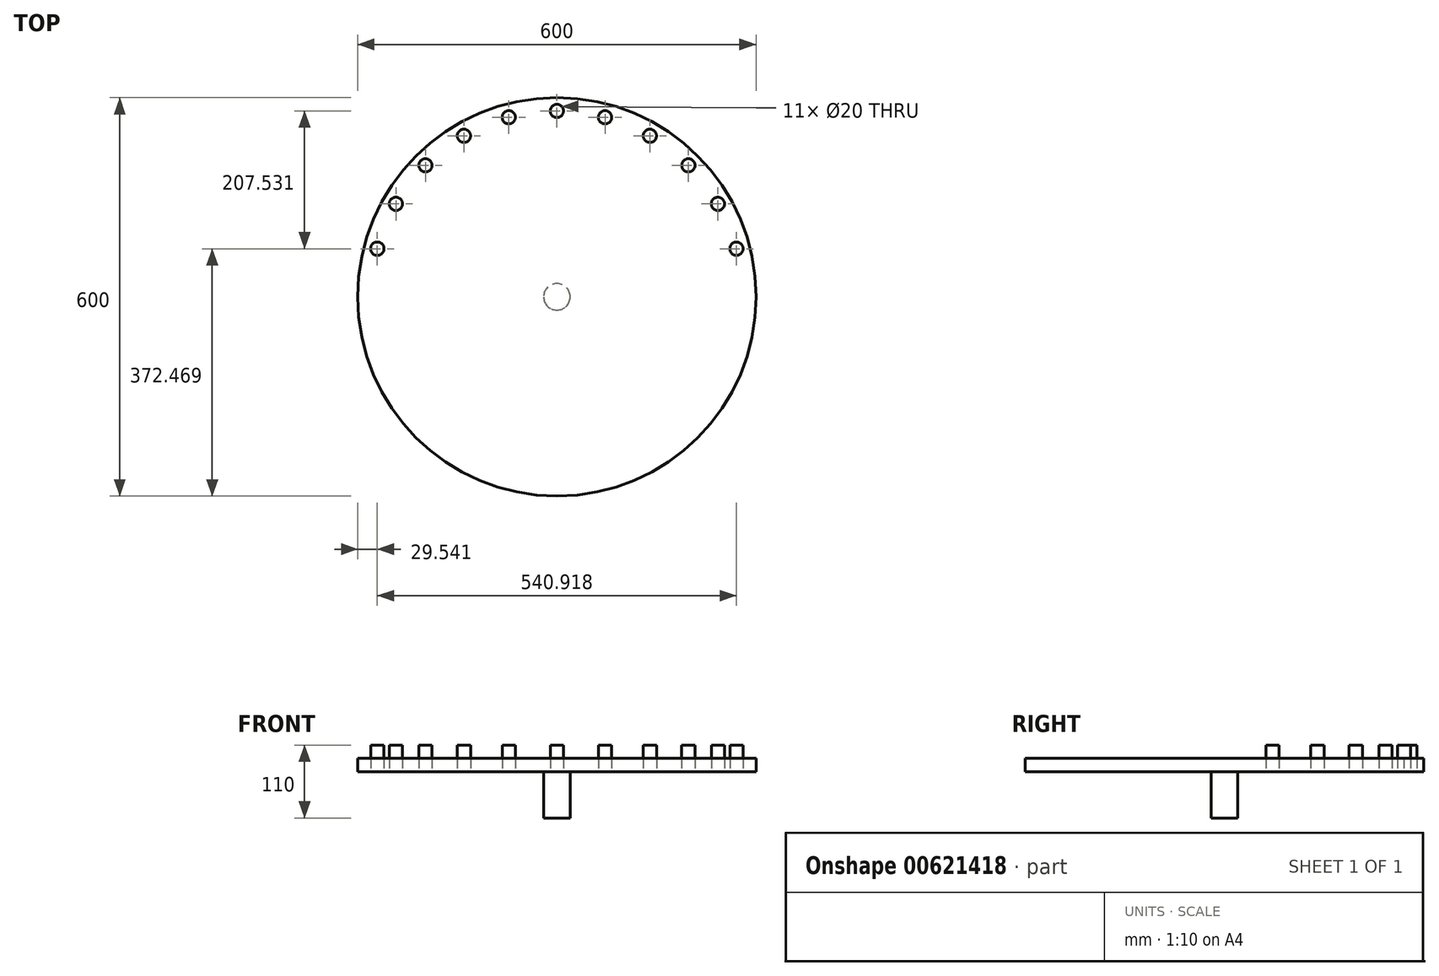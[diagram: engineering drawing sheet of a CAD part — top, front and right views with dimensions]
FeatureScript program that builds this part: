
annotation { "Feature Type Name" : "Feature", "Feature Type Description" : "" }
export const myFeature = defineFeature(function(context is Context, id is Id, definition is map)
    precondition{}
    {
        {
            var Q0;
            Q0=qCreatedBy(makeId("Top.planeOp"),FACE);
            var sketch = newSketch(context, id + "F0", { "sketchPlane" : qUnion([Q0])});
            skCircle(sketch, "E0", {"center": v(0, 0) * mm, "radius": 300 * mm});
            skCircle(sketch, "E1.0", {"center": v(0, 0) * mm, "radius": 280 * mm, "construction": true});
            skLineSegment(sketch, "E2", {"start": v(0, 0) * mm, "end": v(-300, 0) * mm, "construction": true});
            skLineSegment(sketch, "E3", {"start": v(0, 0) * mm, "end": v(-270.46, 72.47) * mm, "construction": true});
            skLineSegment(sketch, "E4", {"start": v(0, 0) * mm, "end": v(-242.49, 140) * mm, "construction": true});
            skLineSegment(sketch, "E5", {"start": v(0, 0) * mm, "end": v(-197.99, 197.99) * mm, "construction": true});
            skLineSegment(sketch, "E6", {"start": v(0, 0) * mm, "end": v(-140, 242.49) * mm, "construction": true});
            skLineSegment(sketch, "E7", {"start": v(0, 0) * mm, "end": v(-72.47, 270.46) * mm, "construction": true});
            skLineSegment(sketch, "E8", {"start": v(0, 0) * mm, "end": v(0, 280) * mm, "construction": true});
            skLineSegment(sketch, "E9.MirrorCS", {"start": v(0, 0) * mm, "end": v(72.47, 270.46) * mm, "construction": true});
            skLineSegment(sketch, "E10.MirrorCS", {"start": v(0, 0) * mm, "end": v(140, 242.49) * mm, "construction": true});
            skLineSegment(sketch, "E11.MirrorCS", {"start": v(0, 0) * mm, "end": v(197.99, 197.99) * mm, "construction": true});
            skLineSegment(sketch, "E12.MirrorCS", {"start": v(0, 0) * mm, "end": v(242.49, 140) * mm, "construction": true});
            skLineSegment(sketch, "E13.MirrorCS", {"start": v(0, 0) * mm, "end": v(270.46, 72.47) * mm, "construction": true});
            skLineSegment(sketch, "E14.MirrorCS", {"start": v(0, 0) * mm, "end": v(300, 0) * mm, "construction": true});
            skCircle(sketch, "E15", {"center": v(-270.46, 72.47) * mm, "radius": 10 * mm});
            skCircle(sketch, "E16", {"center": v(-242.49, 140) * mm, "radius": 10 * mm});
            skCircle(sketch, "E17", {"center": v(-197.99, 197.99) * mm, "radius": 10 * mm});
            skCircle(sketch, "E18", {"center": v(-140, 242.49) * mm, "radius": 10 * mm});
            skCircle(sketch, "E19", {"center": v(-72.47, 270.46) * mm, "radius": 10 * mm});
            skCircle(sketch, "E20", {"center": v(0, 280) * mm, "radius": 10 * mm});
            skCircle(sketch, "E21.MirrorC", {"center": v(270.46, 72.47) * mm, "radius": 10 * mm});
            skCircle(sketch, "E22.MirrorC", {"center": v(242.49, 140) * mm, "radius": 10 * mm});
            skCircle(sketch, "E23.MirrorC", {"center": v(197.99, 197.99) * mm, "radius": 10 * mm});
            skCircle(sketch, "E24.MirrorC", {"center": v(140, 242.49) * mm, "radius": 10 * mm});
            skCircle(sketch, "E25.MirrorC", {"center": v(72.47, 270.46) * mm, "radius": 10 * mm});
            skCircle(sketch, "E26", {"center": v(0, 0) * mm, "radius": 20 * mm});
            skSolve(sketch);
        }
        {
            var Q0;
            Q0=makeQuery(id+"F0.imprint","IMPRINT",FACE,{"disambiguationData":[TD([[makeQuery(id+"F0.imprint","IMPRINT",EDGE,{"derivedFrom":sQuery(id+"F0.wireOp",EDGE,"E0")}),1.0]])]});
            var Q1;
            Q1=sQuery(id+"F0.wireOp",EDGE,"E0");
            extrude(context, id + "F1", {"entities" : qUnion([Q0]), "surfaceEntities" : qUnion([Q1]), "depth" : 20 * mm, "offsetDistance" : 25 * mm});
        }
        {
            var Q0;
            Q0=makeQuery(id+"F1.opExtrude","CAP_FACE",FACE,{"disambiguationData":[OSD([sQuery(id+"F0.wireOp",EDGE,"E0"),sQuery(id+"F0.wireOp",EDGE,"E15"),sQuery(id+"F0.wireOp",EDGE,"E16"),sQuery(id+"F0.wireOp",EDGE,"E17"),sQuery(id+"F0.wireOp",EDGE,"E18"),sQuery(id+"F0.wireOp",EDGE,"E19"),sQuery(id+"F0.wireOp",EDGE,"E20"),sQuery(id+"F0.wireOp",EDGE,"E21.MirrorC"),sQuery(id+"F0.wireOp",EDGE,"E22.MirrorC"),sQuery(id+"F0.wireOp",EDGE,"E23.MirrorC"),sQuery(id+"F0.wireOp",EDGE,"E24.MirrorC"),sQuery(id+"F0.wireOp",EDGE,"E25.MirrorC"),sQuery(id+"F0.wireOp",EDGE,"E26")])],"isStart":false});
            var sketch = newSketch(context, id + "F2", { "sketchPlane" : qUnion([Q0])});
            skCircle(sketch, "E27.0", {"center": v(0, 0) * mm, "radius": 280 * mm, "construction": true});
            skLineSegment(sketch, "E28", {"start": v(0, 0) * mm, "end": v(-300, 0) * mm, "construction": true});
            skLineSegment(sketch, "E29", {"start": v(0, 0) * mm, "end": v(-270.46, 72.47) * mm, "construction": true});
            skLineSegment(sketch, "E30", {"start": v(0, 0) * mm, "end": v(-242.49, 140) * mm, "construction": true});
            skLineSegment(sketch, "E31", {"start": v(0, 0) * mm, "end": v(-197.99, 197.99) * mm, "construction": true});
            skLineSegment(sketch, "E32", {"start": v(0, 0) * mm, "end": v(-140, 242.49) * mm, "construction": true});
            skLineSegment(sketch, "E33", {"start": v(0, 0) * mm, "end": v(-72.47, 270.46) * mm, "construction": true});
            skLineSegment(sketch, "E34", {"start": v(0, 0) * mm, "end": v(0, 280) * mm, "construction": true});
            skLineSegment(sketch, "E35.MirrorCS", {"start": v(0, 0) * mm, "end": v(72.47, 270.46) * mm, "construction": true});
            skLineSegment(sketch, "E36.MirrorCS", {"start": v(0, 0) * mm, "end": v(140, 242.49) * mm, "construction": true});
            skLineSegment(sketch, "E37.MirrorCS", {"start": v(0, 0) * mm, "end": v(197.99, 197.99) * mm, "construction": true});
            skLineSegment(sketch, "E38.MirrorCS", {"start": v(0, 0) * mm, "end": v(242.49, 140) * mm, "construction": true});
            skLineSegment(sketch, "E39.MirrorCS", {"start": v(0, 0) * mm, "end": v(270.46, 72.47) * mm, "construction": true});
            skLineSegment(sketch, "E40.MirrorCS", {"start": v(0, 0) * mm, "end": v(300, 0) * mm, "construction": true});
            skCircle(sketch, "E41", {"center": v(-270.46, 72.47) * mm, "radius": 10 * mm});
            skCircle(sketch, "E42", {"center": v(-242.49, 140) * mm, "radius": 10 * mm});
            skCircle(sketch, "E43", {"center": v(-197.99, 197.99) * mm, "radius": 10 * mm});
            skCircle(sketch, "E44", {"center": v(-140, 242.49) * mm, "radius": 10 * mm});
            skCircle(sketch, "E45", {"center": v(-72.47, 270.46) * mm, "radius": 10 * mm});
            skCircle(sketch, "E46", {"center": v(0, 280) * mm, "radius": 10 * mm});
            skCircle(sketch, "E47.MirrorC", {"center": v(270.46, 72.47) * mm, "radius": 10 * mm});
            skCircle(sketch, "E48.MirrorC", {"center": v(242.49, 140) * mm, "radius": 10 * mm});
            skCircle(sketch, "E49.MirrorC", {"center": v(197.99, 197.99) * mm, "radius": 10 * mm});
            skCircle(sketch, "E50.MirrorC", {"center": v(140, 242.49) * mm, "radius": 10 * mm});
            skCircle(sketch, "E51.MirrorC", {"center": v(72.47, 270.46) * mm, "radius": 10 * mm});
            skSolve(sketch);
        }
        {
            var Q0;
            Q0=qSketchRegion(id+"F2",true);
            extrude(context, id + "F3", {"entities" : qUnion([Q0]), "depth" : 40 * mm, "offsetDistance" : 25 * mm, "symmetric" : true});
        }
        {
            var Q0;
            Q0=makeQuery(id+"F1.opExtrude","CAP_FACE",FACE,{"disambiguationData":[OSD([sQuery(id+"F0.wireOp",EDGE,"E0"),sQuery(id+"F0.wireOp",EDGE,"E15"),sQuery(id+"F0.wireOp",EDGE,"E16"),sQuery(id+"F0.wireOp",EDGE,"E17"),sQuery(id+"F0.wireOp",EDGE,"E18"),sQuery(id+"F0.wireOp",EDGE,"E19"),sQuery(id+"F0.wireOp",EDGE,"E20"),sQuery(id+"F0.wireOp",EDGE,"E21.MirrorC"),sQuery(id+"F0.wireOp",EDGE,"E22.MirrorC"),sQuery(id+"F0.wireOp",EDGE,"E23.MirrorC"),sQuery(id+"F0.wireOp",EDGE,"E24.MirrorC"),sQuery(id+"F0.wireOp",EDGE,"E25.MirrorC"),sQuery(id+"F0.wireOp",EDGE,"E26")])],"isStart":false});
            var sketch = newSketch(context, id + "F4", { "sketchPlane" : qUnion([Q0])});
            skLineSegment(sketch, "E52", {"start": v(0, 0) * mm, "end": v(0, 67.05) * mm, "construction": true});
            skLineSegment(sketch, "E53", {"start": v(0, 0) * mm, "end": v(-65, 0) * mm, "construction": true});
            skLineSegment(sketch, "E54", {"start": v(-65, 0) * mm, "end": v(-65, 20) * mm});
            skLineSegment(sketch, "E55", {"start": v(-65, 20) * mm, "end": v(-20, 20) * mm});
            skLineSegment(sketch, "E56", {"start": v(-20, 20) * mm, "end": v(-20, 65) * mm});
            skLineSegment(sketch, "E57", {"start": v(-20, 65) * mm, "end": v(0, 65) * mm});
            skLineSegment(sketch, "E58.MirrorCS", {"start": v(20, 65) * mm, "end": v(0, 65) * mm});
            skLineSegment(sketch, "E59.MirrorCS", {"start": v(20, 20) * mm, "end": v(20, 65) * mm});
            skLineSegment(sketch, "E60.MirrorCS", {"start": v(65, 20) * mm, "end": v(20, 20) * mm});
            skLineSegment(sketch, "E61.MirrorCS", {"start": v(65, 0) * mm, "end": v(65, 20) * mm});
            skLineSegment(sketch, "E62.MirrorCS", {"start": v(-65, 0) * mm, "end": v(-65, -20) * mm});
            skLineSegment(sketch, "E63.MirrorCS", {"start": v(-65, -20) * mm, "end": v(-20, -20) * mm});
            skLineSegment(sketch, "E64.MirrorCS", {"start": v(-20, -20) * mm, "end": v(-20, -65) * mm});
            skLineSegment(sketch, "E65.MirrorCS", {"start": v(-20, -65) * mm, "end": v(0, -65) * mm});
            skLineSegment(sketch, "E66.MirrorCS", {"start": v(20, -20) * mm, "end": v(20, -65) * mm});
            skLineSegment(sketch, "E67.MirrorCS", {"start": v(20, -65) * mm, "end": v(0, -65) * mm});
            skLineSegment(sketch, "E68.MirrorCS", {"start": v(65, -20) * mm, "end": v(20, -20) * mm});
            skLineSegment(sketch, "E69.MirrorCS", {"start": v(65, 0) * mm, "end": v(65, -20) * mm});
            skSolve(sketch);
        }
        {
            var Q0;
            Q0=qSketchRegion(id+"F4",true);
            extrude(context, id + "F5", {"entities" : qUnion([Q0]), "operationType" : NewBodyOperationType.REMOVE, "oppositeDirection" : true, "depth" : 10 * mm, "offsetDistance" : 25 * mm});
        }
        {
            var Q0;
            Q0=makeQuery(id+"F1.opExtrude","CAP_FACE",FACE,{"disambiguationData":[OSD([sQuery(id+"F0.wireOp",EDGE,"E0"),sQuery(id+"F0.wireOp",EDGE,"E15"),sQuery(id+"F0.wireOp",EDGE,"E16"),sQuery(id+"F0.wireOp",EDGE,"E17"),sQuery(id+"F0.wireOp",EDGE,"E18"),sQuery(id+"F0.wireOp",EDGE,"E19"),sQuery(id+"F0.wireOp",EDGE,"E20"),sQuery(id+"F0.wireOp",EDGE,"E21.MirrorC"),sQuery(id+"F0.wireOp",EDGE,"E22.MirrorC"),sQuery(id+"F0.wireOp",EDGE,"E23.MirrorC"),sQuery(id+"F0.wireOp",EDGE,"E24.MirrorC"),sQuery(id+"F0.wireOp",EDGE,"E25.MirrorC"),sQuery(id+"F0.wireOp",EDGE,"E26")])],"isStart":false});
            var sketch = newSketch(context, id + "F6", { "sketchPlane" : qUnion([Q0])});
            skLineSegment(sketch, "E70", {"start": v(-65, -20) * mm, "end": v(-65, 20) * mm});
            skLineSegment(sketch, "E71", {"start": v(-65, 20) * mm, "end": v(-20, 20) * mm});
            skLineSegment(sketch, "E72", {"start": v(-20, 20) * mm, "end": v(-20, 65) * mm});
            skLineSegment(sketch, "E73", {"start": v(-20, 65) * mm, "end": v(20, 65) * mm});
            skLineSegment(sketch, "E74", {"start": v(20, 65) * mm, "end": v(20, 20) * mm});
            skLineSegment(sketch, "E75", {"start": v(20, 20) * mm, "end": v(65, 20) * mm});
            skLineSegment(sketch, "E76", {"start": v(65, 20) * mm, "end": v(65, -20) * mm});
            skLineSegment(sketch, "E77", {"start": v(65, -20) * mm, "end": v(20, -20) * mm});
            skLineSegment(sketch, "E78", {"start": v(20, -20) * mm, "end": v(20, -65) * mm});
            skLineSegment(sketch, "E79", {"start": v(20, -65) * mm, "end": v(-20, -65) * mm});
            skLineSegment(sketch, "E80", {"start": v(-20, -65) * mm, "end": v(-20, -20) * mm});
            skLineSegment(sketch, "E81", {"start": v(-20, -20) * mm, "end": v(-65, -20) * mm});
            skSolve(sketch);
        }
        {
            var Q0;
            Q0=qSketchRegion(id+"F6",true);
            extrude(context, id + "F7", {"entities" : qUnion([Q0]), "oppositeDirection" : true, "depth" : 10 * mm, "offsetDistance" : 25 * mm});
        }
        {
            var Q0;
            Q0=makeQuery(id+"F7.opExtrude","CAP_FACE",FACE,{"disambiguationData":[OSD([sQuery(id+"F6.wireOp",EDGE,"E70"),sQuery(id+"F6.wireOp",EDGE,"E71"),sQuery(id+"F6.wireOp",EDGE,"E72"),sQuery(id+"F6.wireOp",EDGE,"E73"),sQuery(id+"F6.wireOp",EDGE,"E74"),sQuery(id+"F6.wireOp",EDGE,"E75"),sQuery(id+"F6.wireOp",EDGE,"E76"),sQuery(id+"F6.wireOp",EDGE,"E77"),sQuery(id+"F6.wireOp",EDGE,"E78"),sQuery(id+"F6.wireOp",EDGE,"E79"),sQuery(id+"F6.wireOp",EDGE,"E80"),sQuery(id+"F6.wireOp",EDGE,"E81")])],"isStart":false});
            var sketch = newSketch(context, id + "F8", { "sketchPlane" : qUnion([Q0])});
            skCircle(sketch, "E82", {"center": v(0, 0) * mm, "radius": 20 * mm});
            skSolve(sketch);
        }
        {
            var Q0;
            Q0=qSketchRegion(id+"F8",true);
            extrude(context, id + "F9", {"entities" : qUnion([Q0]), "operationType" : NewBodyOperationType.ADD, "depth" : 80 * mm, "offsetDistance" : 25 * mm});
        }
    });
